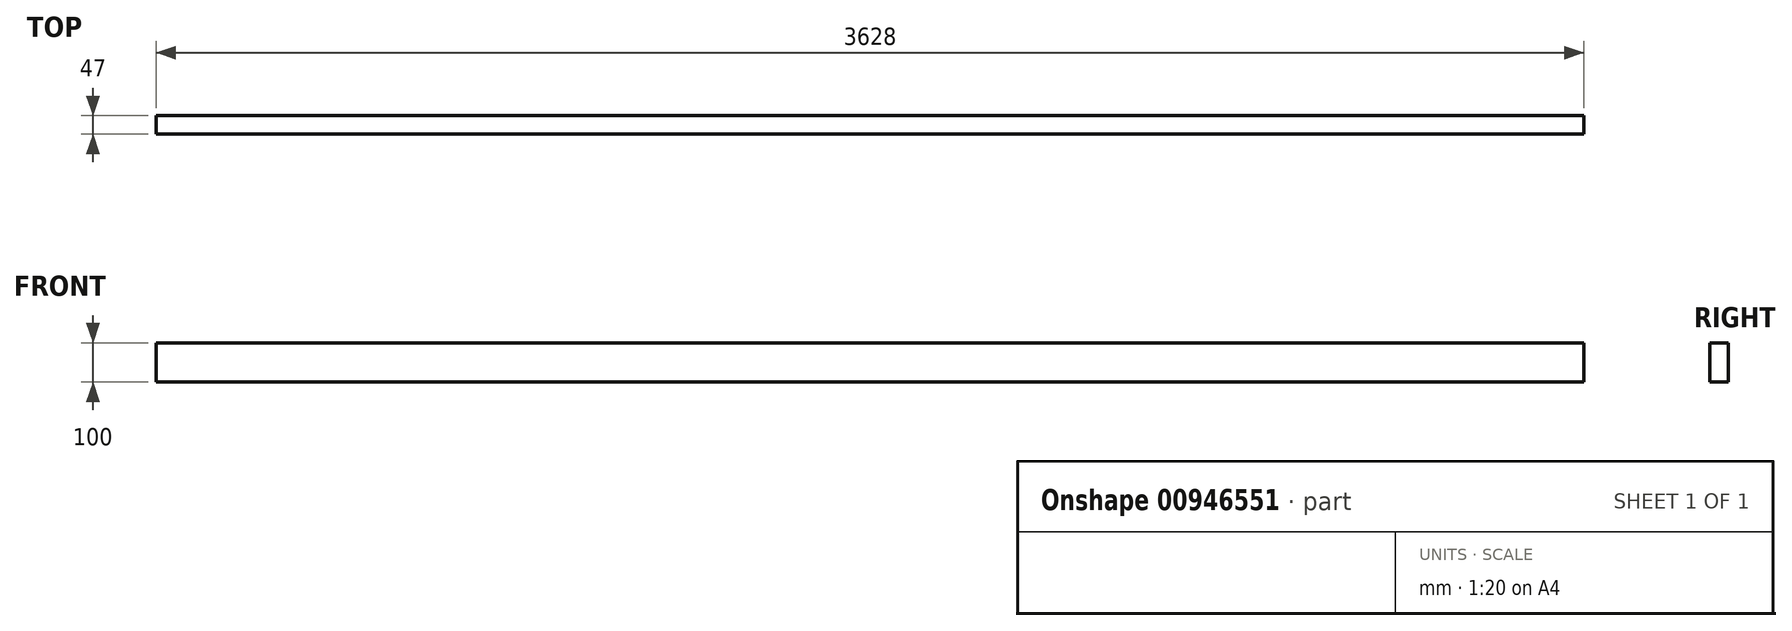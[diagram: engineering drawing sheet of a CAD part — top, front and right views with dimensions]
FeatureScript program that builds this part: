
annotation { "Feature Type Name" : "Feature", "Feature Type Description" : "" }
export const myFeature = defineFeature(function(context is Context, id is Id, definition is map)
    precondition{}
    {
        {
            var Q0;
            Q0=qCreatedBy(makeId("Right.planeOp"),FACE);
            var sketch = newSketch(context, id + "F0", { "sketchPlane" : qUnion([Q0])});
            skLineSegment(sketch, "E0.bottom", {"start": v(0, 0) * mm, "end": v(-47, 0) * mm});
            skLineSegment(sketch, "E0.top", {"start": v(0, 100) * mm, "end": v(-47, 100) * mm});
            skLineSegment(sketch, "E0.left", {"start": v(0, 0) * mm, "end": v(0, 100) * mm});
            skLineSegment(sketch, "E0.right", {"start": v(-47, 0) * mm, "end": v(-47, 100) * mm});
            skSolve(sketch);
        }
        {
            var Q0;
            Q0=qSketchRegion(id+"F0",true);
            extrude(context, id + "F1", {"entities" : qUnion([Q0]), "depth" : 3628 * mm, "offsetDistance" : 25 * mm});
        }
    });
